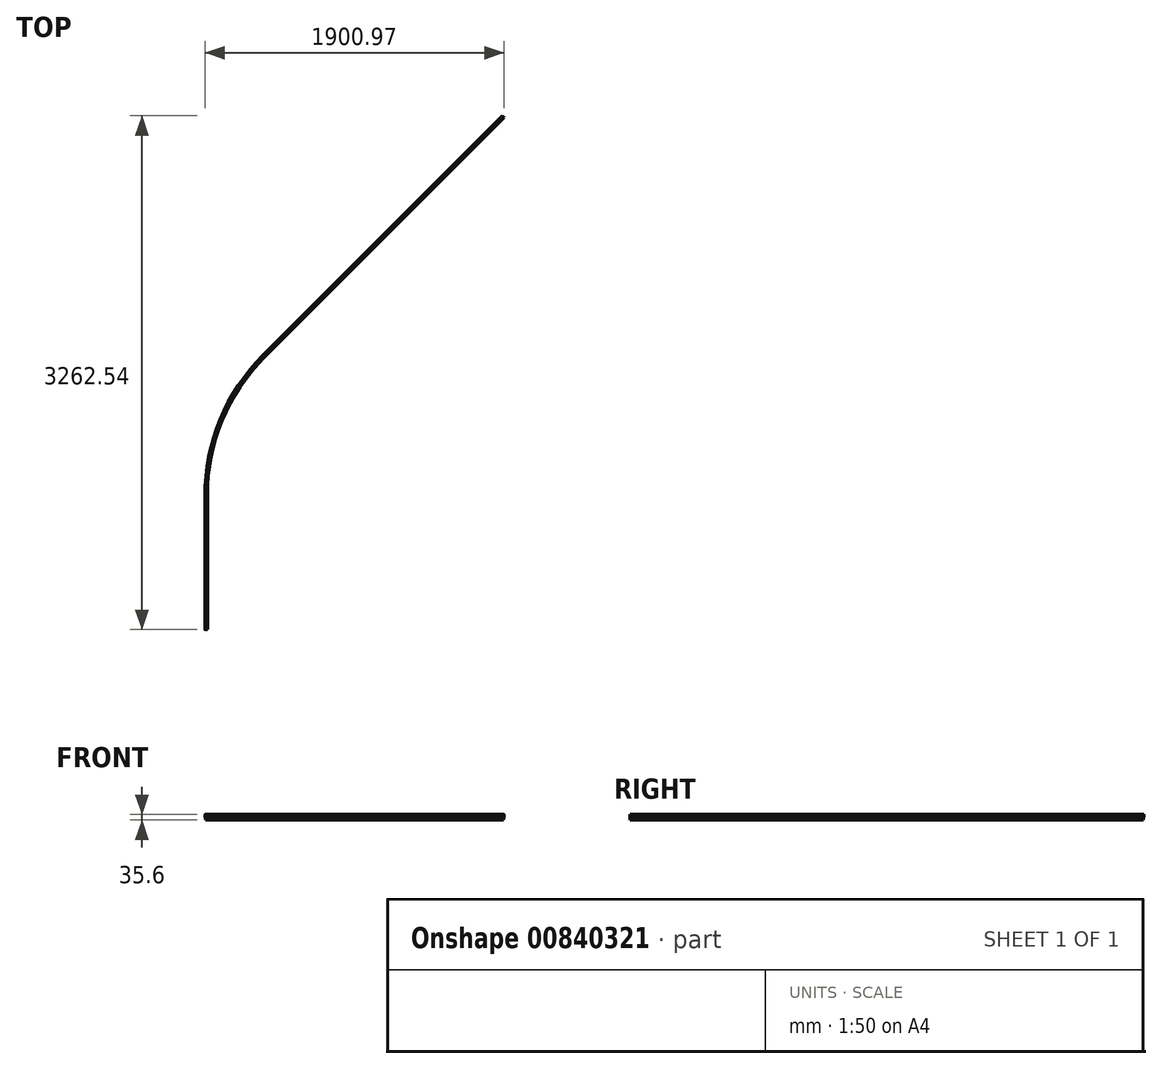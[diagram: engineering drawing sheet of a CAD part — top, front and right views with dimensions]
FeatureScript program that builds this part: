
annotation { "Feature Type Name" : "Feature", "Feature Type Description" : "" }
export const myFeature = defineFeature(function(context is Context, id is Id, definition is map)
    precondition{}
    {
        {
            var Q0;
            Q0=qCreatedBy(makeId("Top.planeOp"),FACE);
            var sketch = newSketch(context, id + "F0", { "sketchPlane" : qUnion([Q0])});
            skLineSegment(sketch, "E0", {"start": v(0, 0) * mm, "end": v(0, 850) * mm});
            skArc(sketch, "E1", {"start": v(366.56, 1734.94) * mm, "mid": v(95.26, 1328.93) * mm, "end": v(0, 850) * mm});
            skLineSegment(sketch, "E2", {"start": v(366.56, 1734.94) * mm, "end": v(1886.84, 3255.22) * mm});
            skLineSegment(sketch, "E3", {"start": v(0, 850) * mm, "end": v(1251.5, 850) * mm, "construction": true});
            skLineSegment(sketch, "E4", {"start": v(366.56, 1734.94) * mm, "end": v(1251.5, 850) * mm, "construction": true});
            skSolve(sketch);
        }
        {
            var Q0;
            Q0=qCreatedBy(makeId("Front.planeOp"),FACE);
            var sketch = newSketch(context, id + "F1", { "sketchPlane" : qUnion([Q0])});
            skLineSegment(sketch, "E5.bottom", {"start": v(0, 15) * mm, "end": v(-5, 15) * mm});
            skLineSegment(sketch, "E5.top", {"start": v(0, -15) * mm, "end": v(-5, -15) * mm});
            skLineSegment(sketch, "E5.left", {"start": v(0, 15) * mm, "end": v(0, -15) * mm});
            skLineSegment(sketch, "E5.right", {"start": v(-5, 15) * mm, "end": v(-5, -15) * mm});
            skSolve(sketch);
        }
        {
            var Q0;
            Q0=makeQuery(id+"F1.imprint","IMPRINT",FACE,{"disambiguationData":[TD([[makeQuery(id+"F1.imprint","IMPRINT",EDGE,{"derivedFrom":sQuery(id+"F1.wireOp",EDGE,"E5.bottom")}),1.0]])]});
            var Q1;
            Q1=sQuery(id+"F0.wireOp",EDGE,"E0");
            var Q2;
            Q2=sQuery(id+"F0.wireOp",EDGE,"E1");
            var Q3;
            Q3=sQuery(id+"F0.wireOp",EDGE,"E2");
            sweep(context, id + "F2", {"profiles" : qUnion([Q0]), "path" : qUnion([Q1, Q2, Q3])});
        }
        {
            var Q0;
            Q0=makeQuery(id+"F2.opSweep","CAP_FACE",FACE,{"disambiguationData":[OSD([sQuery(id+"F0.wireOp",VERTEX,"E0.start"),sQuery(id+"F1.wireOp",EDGE,"E5.bottom"),sQuery(id+"F1.wireOp",EDGE,"E5.top"),sQuery(id+"F1.wireOp",EDGE,"E5.left"),sQuery(id+"F1.wireOp",EDGE,"E5.right")])],"isStart":true});
            var sketch = newSketch(context, id + "F3", { "sketchPlane" : qUnion([Q0])});
            skLineSegment(sketch, "E6", {"start": v(-10.35, 2.8) * mm, "end": v(-10.35, 18.6) * mm});
            skLineSegment(sketch, "E7", {"start": v(-8.35, 20.6) * mm, "end": v(3.35, 20.6) * mm});
            skLineSegment(sketch, "E8", {"start": v(5.35, 18.6) * mm, "end": v(5.35, 2.8) * mm});
            skLineSegment(sketch, "E9", {"start": v(3.35, 0.8) * mm, "end": v(0.05, 0.8) * mm});
            skLineSegment(sketch, "E10", {"start": v(0.05, 0.8) * mm, "end": v(0.05, 15) * mm});
            skLineSegment(sketch, "E11", {"start": v(0.05, 15) * mm, "end": v(-5.05, 15) * mm});
            skLineSegment(sketch, "E12", {"start": v(-5.05, 15) * mm, "end": v(-5.05, 0.8) * mm});
            skLineSegment(sketch, "E13", {"start": v(-5.05, 0.8) * mm, "end": v(-8.35, 0.8) * mm});
            skPoint(sketch, "E14.visualSharp", {"position": v(-10.35, 20.6) * mm});
            skArc(sketch, "E14.filletArc", {"start": v(-8.35, 20.6) * mm, "mid": v(-9.76, 20.01) * mm, "end": v(-10.35, 18.6) * mm});
            skPoint(sketch, "E15.visualSharp", {"position": v(5.35, 20.6) * mm});
            skArc(sketch, "E15.filletArc", {"start": v(5.35, 18.6) * mm, "mid": v(4.76, 20.01) * mm, "end": v(3.35, 20.6) * mm});
            skPoint(sketch, "E16.visualSharp", {"position": v(5.35, 0.8) * mm});
            skArc(sketch, "E16.filletArc", {"start": v(3.35, 0.8) * mm, "mid": v(4.76, 1.39) * mm, "end": v(5.35, 2.8) * mm});
            skPoint(sketch, "E17.visualSharp", {"position": v(-10.35, 0.8) * mm});
            skArc(sketch, "E17.filletArc", {"start": v(-10.35, 2.8) * mm, "mid": v(-9.76, 1.39) * mm, "end": v(-8.35, 0.8) * mm});
            skSolve(sketch);
        }
        {
            var Q0;
            Q0 = qSketchRegion(id + "F3", true);
            var Q1;
            Q1=makeQuery(id+"F2.opSweep","SWEPT_EDGE",EDGE,{"disambiguationData":[OSD([sQuery(id+"F0.wireOp",EDGE,"E0"),sQuery(id+"F1.wireOp",EDGE,"E5.bottom"),sQuery(id+"F1.wireOp",EDGE,"E5.left")])]});
            var Q2;
            Q2=makeQuery(id+"F2.opSweep","SWEPT_EDGE",EDGE,{"disambiguationData":[OSD([sQuery(id+"F0.wireOp",EDGE,"E1"),sQuery(id+"F1.wireOp",EDGE,"E5.bottom"),sQuery(id+"F1.wireOp",EDGE,"E5.left")])]});
            var Q3;
            Q3=makeQuery(id+"F2.opSweep","SWEPT_EDGE",EDGE,{"disambiguationData":[OSD([sQuery(id+"F0.wireOp",EDGE,"E2"),sQuery(id+"F1.wireOp",EDGE,"E5.bottom"),sQuery(id+"F1.wireOp",EDGE,"E5.left")])]});
            sweep(context, id + "F4", {"profiles" : qUnion([Q0]), "path" : qUnion([Q1, Q2, Q3])});
        }
    });
